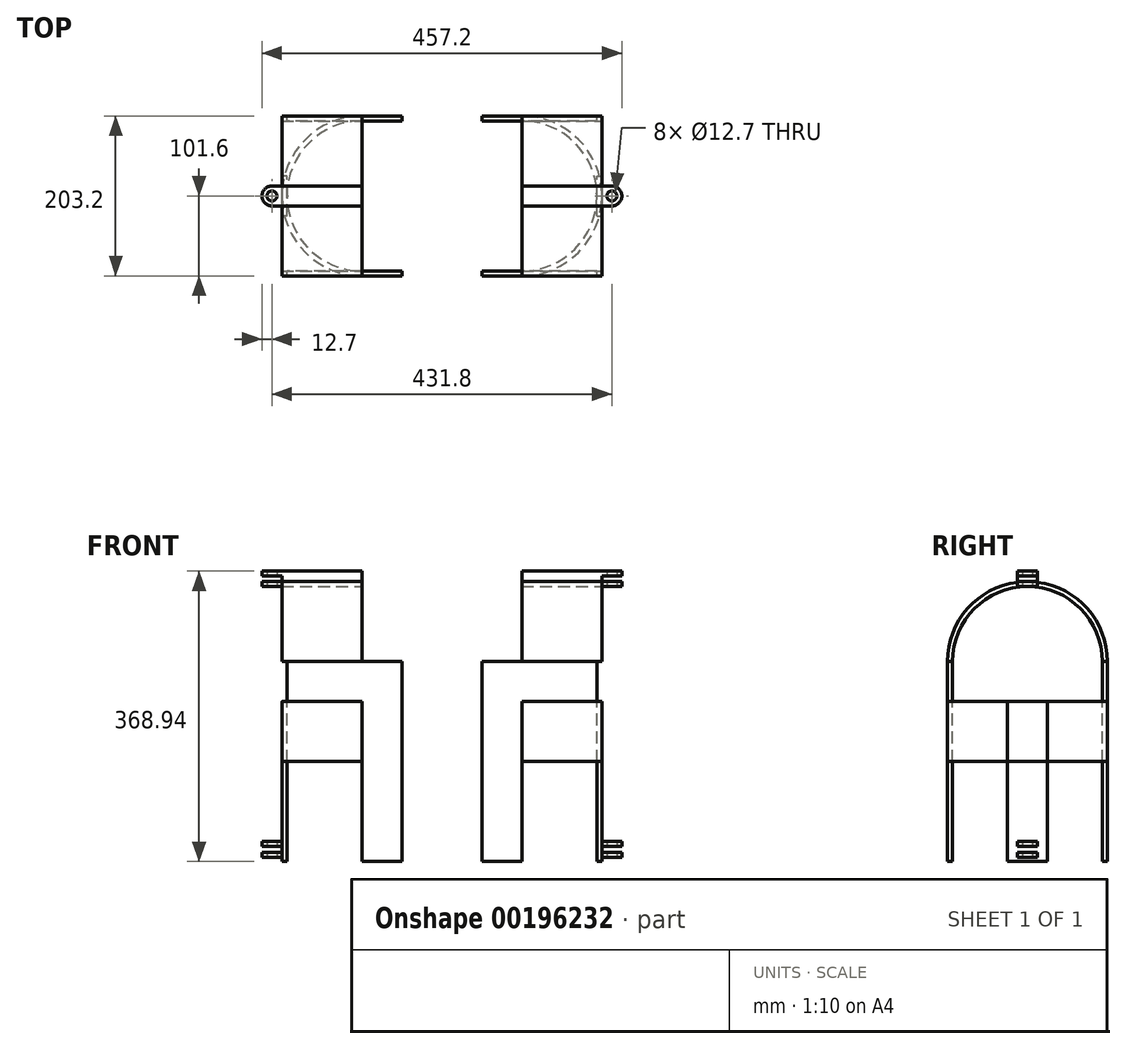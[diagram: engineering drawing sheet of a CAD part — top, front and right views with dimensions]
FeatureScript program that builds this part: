
annotation { "Feature Type Name" : "Feature", "Feature Type Description" : "" }
export const myFeature = defineFeature(function(context is Context, id is Id, definition is map)
    precondition{}
    {
        {
            var Q0;
            Q0=qCreatedBy(makeId("Front.planeOp"),FACE);
            var sketch = newSketch(context, id + "F0", { "sketchPlane" : qUnion([Q0])});
            skLineSegment(sketch, "E0", {"start": v(0, 0) * mm, "end": v(203.2, 0) * mm});
            skLineSegment(sketch, "E1", {"start": v(0, 0) * mm, "end": v(-203.2, 0) * mm});
            skLineSegment(sketch, "E2", {"start": v(0, 0) * mm, "end": v(0, 406.4) * mm});
            skLineSegment(sketch, "E3", {"start": v(0, 406.4) * mm, "end": v(203.2, 406.4) * mm});
            skLineSegment(sketch, "E4", {"start": v(203.2, 406.4) * mm, "end": v(203.2, 0) * mm});
            skLineSegment(sketch, "E5", {"start": v(0, 406.4) * mm, "end": v(-203.2, 406.4) * mm});
            skLineSegment(sketch, "E6", {"start": v(-203.2, 406.4) * mm, "end": v(-203.2, 0) * mm});
            skLineSegment(sketch, "E7", {"start": v(-101.6, 406.4) * mm, "end": v(-101.6, 0) * mm});
            skLineSegment(sketch, "E8", {"start": v(101.6, 0) * mm, "end": v(101.6, 406.4) * mm});
            skLineSegment(sketch, "E9", {"start": v(203.2, 406.4) * mm, "end": v(304.8, 406.4) * mm});
            skLineSegment(sketch, "E10", {"start": v(304.8, 406.4) * mm, "end": v(304.8, 304.8) * mm});
            skLineSegment(sketch, "E11", {"start": v(304.8, 304.8) * mm, "end": v(203.2, 304.8) * mm});
            skLineSegment(sketch, "E12", {"start": v(203.2, 304.8) * mm, "end": v(203.2, 406.4) * mm});
            skLineSegment(sketch, "E13", {"start": v(-203.2, 406.4) * mm, "end": v(-304.8, 406.4) * mm});
            skLineSegment(sketch, "E14", {"start": v(-304.8, 406.4) * mm, "end": v(-304.8, 304.8) * mm});
            skLineSegment(sketch, "E15", {"start": v(-304.8, 304.8) * mm, "end": v(-203.2, 304.8) * mm});
            skLineSegment(sketch, "E16", {"start": v(-203.2, 304.8) * mm, "end": v(-203.2, 406.4) * mm});
            skLineSegment(sketch, "E17", {"start": v(0, 0) * mm, "end": v(0, 50.8) * mm});
            skLineSegment(sketch, "E18", {"start": v(0, 50.8) * mm, "end": v(0, 127) * mm});
            skLineSegment(sketch, "E19", {"start": v(0, 127) * mm, "end": v(0, 177.8) * mm});
            skLineSegment(sketch, "E20", {"start": v(203.2, 304.8) * mm, "end": v(-203.2, 304.8) * mm});
            skLineSegment(sketch, "E21", {"start": v(0, 177.8) * mm, "end": v(0, 254) * mm});
            skLineSegment(sketch, "E22", {"start": v(0, 254) * mm, "end": v(0, 304.8) * mm});
            skLineSegment(sketch, "E23", {"start": v(0, 50.8) * mm, "end": v(-203.2, 50.8) * mm});
            skLineSegment(sketch, "E24", {"start": v(0, 50.8) * mm, "end": v(203.2, 50.8) * mm});
            skLineSegment(sketch, "E25", {"start": v(0, 127) * mm, "end": v(203.2, 127) * mm});
            skLineSegment(sketch, "E26", {"start": v(0, 127) * mm, "end": v(-203.2, 127) * mm});
            skLineSegment(sketch, "E27", {"start": v(0, 177.8) * mm, "end": v(203.2, 177.8) * mm});
            skLineSegment(sketch, "E28", {"start": v(0, 177.8) * mm, "end": v(-203.2, 177.8) * mm});
            skLineSegment(sketch, "E29", {"start": v(0, 254) * mm, "end": v(203.2, 254) * mm});
            skLineSegment(sketch, "E30", {"start": v(0, 254) * mm, "end": v(-203.2, 254) * mm});
            skLineSegment(sketch, "E31", {"start": v(203.2, 0) * mm, "end": v(196.85, 0) * mm});
            skLineSegment(sketch, "E32", {"start": v(196.85, 0) * mm, "end": v(196.85, 304.8) * mm});
            skLineSegment(sketch, "E33", {"start": v(196.85, 304.8) * mm, "end": v(203.2, 304.8) * mm});
            skLineSegment(sketch, "E34", {"start": v(-203.2, 0) * mm, "end": v(-196.85, 0) * mm});
            skLineSegment(sketch, "E35", {"start": v(-196.85, 0) * mm, "end": v(-196.85, 304.8) * mm});
            skLineSegment(sketch, "E36", {"start": v(-196.85, 304.8) * mm, "end": v(-203.2, 304.8) * mm});
            skLineSegment(sketch, "E37", {"start": v(-101.6, 0) * mm, "end": v(-50.8, 0) * mm});
            skLineSegment(sketch, "E38", {"start": v(-50.8, 0) * mm, "end": v(-50.8, 406.4) * mm});
            skLineSegment(sketch, "E39", {"start": v(-50.8, 406.4) * mm, "end": v(-101.6, 406.4) * mm});
            skLineSegment(sketch, "E40", {"start": v(101.6, 406.4) * mm, "end": v(50.8, 406.4) * mm});
            skLineSegment(sketch, "E41", {"start": v(50.8, 406.4) * mm, "end": v(50.8, 0) * mm});
            skLineSegment(sketch, "E42", {"start": v(50.8, 0) * mm, "end": v(101.6, 0) * mm});
            skLineSegment(sketch, "E43", {"start": v(-304.8, 406.4) * mm, "end": v(-304.8, 400.05) * mm});
            skLineSegment(sketch, "E44", {"start": v(-304.8, 400.05) * mm, "end": v(304.8, 400.05) * mm});
            skLineSegment(sketch, "E45", {"start": v(304.8, 400.05) * mm, "end": v(304.8, 406.4) * mm});
            skLineSegment(sketch, "E46.bottom", {"start": v(-304.8, 406.4) * mm, "end": v(-330.2, 406.4) * mm});
            skLineSegment(sketch, "E46.top", {"start": v(-304.8, 400.05) * mm, "end": v(-330.2, 400.05) * mm});
            skLineSegment(sketch, "E46.right", {"start": v(-330.2, 406.4) * mm, "end": v(-330.2, 400.05) * mm});
            skLineSegment(sketch, "E47.bottom", {"start": v(304.8, 406.4) * mm, "end": v(330.2, 406.4) * mm});
            skLineSegment(sketch, "E47.top", {"start": v(304.8, 400.05) * mm, "end": v(330.2, 400.05) * mm});
            skLineSegment(sketch, "E47.left", {"start": v(304.8, 406.4) * mm, "end": v(304.8, 400.05) * mm});
            skLineSegment(sketch, "E47.right", {"start": v(330.2, 406.4) * mm, "end": v(330.2, 400.05) * mm});
            skLineSegment(sketch, "E48", {"start": v(-203.2, 406.4) * mm, "end": v(-203.2, 413.38) * mm});
            skLineSegment(sketch, "E49", {"start": v(-203.2, 413.38) * mm, "end": v(-304.8, 413.38) * mm});
            skLineSegment(sketch, "E50", {"start": v(-304.8, 413.38) * mm, "end": v(-304.8, 406.4) * mm});
            skLineSegment(sketch, "E51.bottom", {"start": v(-203.2, 413.38) * mm, "end": v(-330.2, 413.38) * mm});
            skLineSegment(sketch, "E51.top", {"start": v(-203.2, 419.74) * mm, "end": v(-330.2, 419.74) * mm});
            skLineSegment(sketch, "E51.left", {"start": v(-203.2, 413.38) * mm, "end": v(-203.2, 419.74) * mm});
            skLineSegment(sketch, "E51.right", {"start": v(-330.2, 413.38) * mm, "end": v(-330.2, 419.74) * mm});
            skLineSegment(sketch, "E52", {"start": v(-203.2, 419.74) * mm, "end": v(-101.6, 406.4) * mm});
            skLineSegment(sketch, "E53", {"start": v(203.2, 406.4) * mm, "end": v(203.2, 413.39) * mm});
            skLineSegment(sketch, "E54", {"start": v(203.2, 413.39) * mm, "end": v(304.8, 413.39) * mm});
            skLineSegment(sketch, "E55", {"start": v(304.8, 413.39) * mm, "end": v(304.8, 406.4) * mm});
            skLineSegment(sketch, "E56.bottom", {"start": v(203.2, 413.39) * mm, "end": v(330.2, 413.39) * mm});
            skLineSegment(sketch, "E56.top", {"start": v(203.2, 419.74) * mm, "end": v(330.2, 419.74) * mm});
            skLineSegment(sketch, "E56.left", {"start": v(203.2, 413.39) * mm, "end": v(203.2, 419.74) * mm});
            skLineSegment(sketch, "E56.right", {"start": v(330.2, 413.39) * mm, "end": v(330.2, 419.74) * mm});
            skLineSegment(sketch, "E57", {"start": v(203.2, 419.74) * mm, "end": v(101.6, 406.4) * mm});
            skLineSegment(sketch, "E58", {"start": v(-203.2, 76.2) * mm, "end": v(-203.2, 50.8) * mm});
            skLineSegment(sketch, "E59", {"start": v(-203.2, 50.8) * mm, "end": v(-203.2, 63.5) * mm});
            skLineSegment(sketch, "E60.left", {"start": v(203.2, 50.8) * mm, "end": v(203.2, 76.2) * mm});
            skSolve(sketch);
        }
        {
            var Q0;
            {var subQ0=sQuery(id+"F0.wireOp",EDGE,"E22");Q0=makeQuery(id+"F0.imprint","IMPRINT",FACE,{"disambiguationData":[TD([[makeQuery(id+"F0.imprint","IMPRINT",EDGE,{"derivedFrom":subQ0}),-1.0]])]});}
            var Q1;
            {var subQ0=sQuery(id+"F0.wireOp",EDGE,"E22");Q1=makeQuery(id+"F0.imprint","IMPRINT",FACE,{"disambiguationData":[TD([[makeQuery(id+"F0.imprint","IMPRINT",EDGE,{"derivedFrom":subQ0}),1.0]])]});}
            var Q2;
            {var subQ0=sQuery(id+"F0.wireOp",EDGE,"E20");var subQ1=sQuery(id+"F0.wireOp",EDGE,"E7");var subQ2=makeQuery(id+"F0.imprint","INTERSECT",VERTEX,{"derivedFrom":[subQ1,subQ0]});Q2=makeQuery(id+"F0.imprint","IMPRINT",FACE,{"disambiguationData":[TD([[makeQuery(id+"F0.imprint","IMPRINT",EDGE,{"disambiguationData":[TD([[subQ2,-1.0]])],"derivedFrom":subQ1}),1.0]])]});}
            var Q3;
            {var subQ0=sQuery(id+"F0.wireOp",EDGE,"E30");var subQ1=sQuery(id+"F0.wireOp",EDGE,"E7");var subQ2=makeQuery(id+"F0.imprint","INTERSECT",VERTEX,{"derivedFrom":[subQ1,subQ0]});Q3=makeQuery(id+"F0.imprint","IMPRINT",FACE,{"disambiguationData":[TD([[makeQuery(id+"F0.imprint","IMPRINT",EDGE,{"disambiguationData":[TD([[subQ2,-1.0]])],"derivedFrom":subQ1}),1.0]])]});}
            var Q4;
            {var subQ0=sQuery(id+"F0.wireOp",EDGE,"E29");var subQ1=sQuery(id+"F0.wireOp",EDGE,"E8");var subQ2=makeQuery(id+"F0.imprint","INTERSECT",VERTEX,{"derivedFrom":[subQ1,subQ0]});Q4=makeQuery(id+"F0.imprint","IMPRINT",FACE,{"disambiguationData":[TD([[makeQuery(id+"F0.imprint","IMPRINT",EDGE,{"disambiguationData":[TD([[subQ2,-1.0]])],"derivedFrom":subQ1}),1.0]])]});}
            var Q5;
            {var subQ0=sQuery(id+"F0.wireOp",EDGE,"E27");var subQ1=sQuery(id+"F0.wireOp",EDGE,"E8");var subQ2=makeQuery(id+"F0.imprint","INTERSECT",VERTEX,{"derivedFrom":[subQ1,subQ0]});Q5=makeQuery(id+"F0.imprint","IMPRINT",FACE,{"disambiguationData":[TD([[makeQuery(id+"F0.imprint","IMPRINT",EDGE,{"disambiguationData":[TD([[subQ2,-1.0]])],"derivedFrom":subQ1}),1.0]])]});}
            var Q6;
            {var subQ0=sQuery(id+"F0.wireOp",EDGE,"E25");var subQ1=sQuery(id+"F0.wireOp",EDGE,"E8");var subQ2=makeQuery(id+"F0.imprint","INTERSECT",VERTEX,{"derivedFrom":[subQ1,subQ0]});Q6=makeQuery(id+"F0.imprint","IMPRINT",FACE,{"disambiguationData":[TD([[makeQuery(id+"F0.imprint","IMPRINT",EDGE,{"disambiguationData":[TD([[subQ2,-1.0]])],"derivedFrom":subQ1}),1.0]])]});}
            var Q7;
            {var subQ0=sQuery(id+"F0.wireOp",EDGE,"E19");Q7=makeQuery(id+"F0.imprint","IMPRINT",FACE,{"disambiguationData":[TD([[makeQuery(id+"F0.imprint","IMPRINT",EDGE,{"derivedFrom":subQ0}),-1.0]])]});}
            var Q8;
            {var subQ0=sQuery(id+"F0.wireOp",EDGE,"E19");Q8=makeQuery(id+"F0.imprint","IMPRINT",FACE,{"disambiguationData":[TD([[makeQuery(id+"F0.imprint","IMPRINT",EDGE,{"derivedFrom":subQ0}),1.0]])]});}
            var Q9;
            {var subQ0=sQuery(id+"F0.wireOp",EDGE,"E28");var subQ1=sQuery(id+"F0.wireOp",EDGE,"E7");var subQ2=makeQuery(id+"F0.imprint","INTERSECT",VERTEX,{"derivedFrom":[subQ1,subQ0]});Q9=makeQuery(id+"F0.imprint","IMPRINT",FACE,{"disambiguationData":[TD([[makeQuery(id+"F0.imprint","IMPRINT",EDGE,{"disambiguationData":[TD([[subQ2,-1.0]])],"derivedFrom":subQ1}),1.0]])]});}
            var Q10;
            {var subQ0=sQuery(id+"F0.wireOp",EDGE,"E26");var subQ1=sQuery(id+"F0.wireOp",EDGE,"E7");var subQ2=makeQuery(id+"F0.imprint","INTERSECT",VERTEX,{"derivedFrom":[subQ1,subQ0]});Q10=makeQuery(id+"F0.imprint","IMPRINT",FACE,{"disambiguationData":[TD([[makeQuery(id+"F0.imprint","IMPRINT",EDGE,{"disambiguationData":[TD([[subQ2,-1.0]])],"derivedFrom":subQ1}),1.0]])]});}
            var Q11;
            {var subQ0=sQuery(id+"F0.wireOp",EDGE,"E24");var subQ1=sQuery(id+"F0.wireOp",EDGE,"E8");var subQ2=makeQuery(id+"F0.imprint","INTERSECT",VERTEX,{"derivedFrom":[subQ1,subQ0]});Q11=makeQuery(id+"F0.imprint","IMPRINT",FACE,{"disambiguationData":[TD([[makeQuery(id+"F0.imprint","IMPRINT",EDGE,{"disambiguationData":[TD([[subQ2,-1.0]])],"derivedFrom":subQ1}),1.0]])]});}
            var Q12;
            {var subQ0=sQuery(id+"F0.wireOp",EDGE,"E42");Q12=makeQuery(id+"F0.imprint","IMPRINT",FACE,{"disambiguationData":[TD([[makeQuery(id+"F0.imprint","IMPRINT",EDGE,{"derivedFrom":subQ0}),1.0]])]});}
            var Q13;
            {var subQ0=sQuery(id+"F0.wireOp",EDGE,"E17");Q13=makeQuery(id+"F0.imprint","IMPRINT",FACE,{"disambiguationData":[TD([[makeQuery(id+"F0.imprint","IMPRINT",EDGE,{"derivedFrom":subQ0}),-1.0]])]});}
            var Q14;
            {var subQ0=sQuery(id+"F0.wireOp",EDGE,"E17");Q14=makeQuery(id+"F0.imprint","IMPRINT",FACE,{"disambiguationData":[TD([[makeQuery(id+"F0.imprint","IMPRINT",EDGE,{"derivedFrom":subQ0}),1.0]])]});}
            var Q15;
            {var subQ0=sQuery(id+"F0.wireOp",EDGE,"E37");Q15=makeQuery(id+"F0.imprint","IMPRINT",FACE,{"disambiguationData":[TD([[makeQuery(id+"F0.imprint","IMPRINT",EDGE,{"derivedFrom":subQ0}),1.0]])]});}
            var Q16;
            {var subQ0=sQuery(id+"F0.wireOp",EDGE,"E29");var subQ1=sQuery(id+"F0.wireOp",EDGE,"E8");var subQ2=makeQuery(id+"F0.imprint","INTERSECT",VERTEX,{"derivedFrom":[subQ1,subQ0]});Q16=makeQuery(id+"F0.imprint","IMPRINT",FACE,{"disambiguationData":[TD([[makeQuery(id+"F0.imprint","IMPRINT",EDGE,{"disambiguationData":[TD([[subQ2,-1.0]])],"derivedFrom":subQ1}),-1.0]])]});}
            var Q17;
            {var subQ0=sQuery(id+"F0.wireOp",EDGE,"E20");var subQ1=sQuery(id+"F0.wireOp",EDGE,"E7");var subQ2=makeQuery(id+"F0.imprint","INTERSECT",VERTEX,{"derivedFrom":[subQ1,subQ0]});Q17=makeQuery(id+"F0.imprint","IMPRINT",FACE,{"disambiguationData":[TD([[makeQuery(id+"F0.imprint","IMPRINT",EDGE,{"disambiguationData":[TD([[subQ2,-1.0]])],"derivedFrom":subQ1}),-1.0]])]});}
            extrude(context, id + "F1", {"entities" : qUnion([Q0, Q1, Q2, Q3, Q4, Q5, Q6, Q7, Q8, Q9, Q10, Q11, Q12, Q13, Q14, Q15, Q16, Q17]), "endBound" : BoundingType.SYMMETRIC, "depth" : 6.35 * mm});
        }
        {
            var Q0;
            {var subQ0=sQuery(id+"F0.wireOp",EDGE,"E34");Q0=makeQuery(id+"F0.imprint","IMPRINT",FACE,{"disambiguationData":[TD([[makeQuery(id+"F0.imprint","IMPRINT",EDGE,{"derivedFrom":subQ0}),1.0]])]});}
            var Q1;
            {var subQ0=sQuery(id+"F0.wireOp",EDGE,"E28");var subQ1=sQuery(id+"F0.wireOp",EDGE,"E6");var subQ2=makeQuery(id+"F0.imprint","INTERSECT",VERTEX,{"derivedFrom":[subQ1,subQ0]});Q1=makeQuery(id+"F0.imprint","IMPRINT",FACE,{"disambiguationData":[TD([[makeQuery(id+"F0.imprint","IMPRINT",EDGE,{"disambiguationData":[TD([[subQ2,1.0]])],"derivedFrom":subQ1}),1.0]])]});}
            var Q2;
            Q2=sQuery(id+"F0.wireOp",EDGE,"E7");
            revolve(context, id + "F2", {"entities" : qUnion([Q0, Q1]), "axis" : qUnion([Q2]), "revolveType" : RevolveType.SYMMETRIC, "angle" : 180 * degree});
        }
        {
            var Q0;
            Q0=makeQuery(id+"F1.opExtrude","SWEPT_BODY",BODY,{"disambiguationData":[OSD([sQuery(id+"F0.wireOp",EDGE,"E0"),sQuery(id+"F0.wireOp",EDGE,"E1"),sQuery(id+"F0.wireOp",EDGE,"E7"),sQuery(id+"F0.wireOp",EDGE,"E8"),sQuery(id+"F0.wireOp",EDGE,"E20"),sQuery(id+"F0.wireOp",EDGE,"E23"),sQuery(id+"F0.wireOp",EDGE,"E24"),sQuery(id+"F0.wireOp",EDGE,"E25"),sQuery(id+"F0.wireOp",EDGE,"E26"),sQuery(id+"F0.wireOp",EDGE,"E27"),sQuery(id+"F0.wireOp",EDGE,"E28"),sQuery(id+"F0.wireOp",EDGE,"E29"),sQuery(id+"F0.wireOp",EDGE,"E30"),sQuery(id+"F0.wireOp",EDGE,"E37"),sQuery(id+"F0.wireOp",EDGE,"E38"),sQuery(id+"F0.wireOp",EDGE,"E41"),sQuery(id+"F0.wireOp",EDGE,"E42")])]});
            transform(context, id + "F3", {"entities" : qUnion([Q0]), "transformType" : TransformType.TRANSLATION_3D, "dx" : 0 * mm, "dy" : -98.42 * mm, "dz" : 0 * mm, "makeCopy" : true});
        }
        {
            var Q0;
            Q0=makeQuery(id+"F1.opExtrude","SWEPT_BODY",BODY,{"disambiguationData":[OSD([sQuery(id+"F0.wireOp",EDGE,"E0"),sQuery(id+"F0.wireOp",EDGE,"E1"),sQuery(id+"F0.wireOp",EDGE,"E7"),sQuery(id+"F0.wireOp",EDGE,"E8"),sQuery(id+"F0.wireOp",EDGE,"E20"),sQuery(id+"F0.wireOp",EDGE,"E23"),sQuery(id+"F0.wireOp",EDGE,"E24"),sQuery(id+"F0.wireOp",EDGE,"E25"),sQuery(id+"F0.wireOp",EDGE,"E26"),sQuery(id+"F0.wireOp",EDGE,"E27"),sQuery(id+"F0.wireOp",EDGE,"E28"),sQuery(id+"F0.wireOp",EDGE,"E29"),sQuery(id+"F0.wireOp",EDGE,"E30"),sQuery(id+"F0.wireOp",EDGE,"E37"),sQuery(id+"F0.wireOp",EDGE,"E38"),sQuery(id+"F0.wireOp",EDGE,"E41"),sQuery(id+"F0.wireOp",EDGE,"E42")])]});
            transform(context, id + "F4", {"entities" : qUnion([Q0]), "transformType" : TransformType.TRANSLATION_3D, "dx" : 0 * mm, "dy" : 98.42 * mm, "dz" : 0 * mm, "makeCopy" : false});
        }
        {
            var Q0;
            {var subQ0=sQuery(id+"F0.wireOp",EDGE,"E31");Q0=makeQuery(id+"F0.imprint","IMPRINT",FACE,{"disambiguationData":[TD([[makeQuery(id+"F0.imprint","IMPRINT",EDGE,{"derivedFrom":subQ0}),-1.0]])]});}
            var Q1;
            {var subQ0=sQuery(id+"F0.wireOp",EDGE,"E27");var subQ1=sQuery(id+"F0.wireOp",EDGE,"E4");var subQ2=makeQuery(id+"F0.imprint","INTERSECT",VERTEX,{"derivedFrom":[subQ1,subQ0]});Q1=makeQuery(id+"F0.imprint","IMPRINT",FACE,{"disambiguationData":[TD([[makeQuery(id+"F0.imprint","IMPRINT",EDGE,{"disambiguationData":[TD([[subQ2,1.0]])],"derivedFrom":subQ1}),-1.0]])]});}
            var Q2;
            Q2=sQuery(id+"F0.wireOp",EDGE,"E8");
            revolve(context, id + "F5", {"entities" : qUnion([Q0, Q1]), "axis" : qUnion([Q2]), "revolveType" : RevolveType.SYMMETRIC, "angle" : 180 * degree});
        }
        {
            var Q0;
            {var subQ3=sQuery(id+"F0.wireOp",EDGE,"E7");var subQ5=sQuery(id+"F0.wireOp",EDGE,"E44");var subQ7=makeQuery(id+"F0.imprint","INTERSECT",VERTEX,{"derivedFrom":[subQ3,subQ5]});Q0=makeQuery(id+"F0.imprint","IMPRINT",FACE,{"disambiguationData":[TD([[makeQuery(id+"F0.imprint","IMPRINT",EDGE,{"disambiguationData":[TD([[subQ7,1.0]])],"derivedFrom":subQ5}),1.0]])]});}
            var Q1;
            {var subQ3=sQuery(id+"F0.wireOp",EDGE,"E8");var subQ5=sQuery(id+"F0.wireOp",EDGE,"E44");var subQ6=makeQuery(id+"F0.imprint","INTERSECT",VERTEX,{"derivedFrom":[subQ3,subQ5]});Q1=makeQuery(id+"F0.imprint","IMPRINT",FACE,{"disambiguationData":[TD([[makeQuery(id+"F0.imprint","IMPRINT",EDGE,{"disambiguationData":[TD([[subQ6,-1.0]])],"derivedFrom":subQ5}),1.0]])]});}
            var Q2;
            Q2=sQuery(id+"F0.wireOp",EDGE,"E20");
            revolve(context, id + "F6", {"entities" : qUnion([Q0, Q1]), "axis" : qUnion([Q2]), "revolveType" : RevolveType.SYMMETRIC, "angle" : 180 * degree});
        }
        {
            var Q0;
            Q0=makeQuery(id+"F0.imprint","IMPRINT",FACE,{"disambiguationData":[TD([[makeQuery(id+"F0.imprint","IMPRINT",EDGE,{"derivedFrom":sQuery(id+"F0.wireOp",EDGE,"E47.bottom")}),-1.0]])]});
            var Q1;
            Q1=makeQuery(id+"F0.imprint","IMPRINT",FACE,{"disambiguationData":[TD([[makeQuery(id+"F0.imprint","IMPRINT",EDGE,{"derivedFrom":sQuery(id+"F0.wireOp",EDGE,"E46.bottom")}),1.0]])]});
            var Q2;
            Q2=makeQuery(id+"F0.imprint","IMPRINT",FACE,{"disambiguationData":[TD([[makeQuery(id+"F0.imprint","IMPRINT",EDGE,{"derivedFrom":sQuery(id+"F0.wireOp",EDGE,"E13")}),-1.0]])]});
            var Q3;
            Q3=makeQuery(id+"F0.imprint","IMPRINT",FACE,{"disambiguationData":[TD([[makeQuery(id+"F0.imprint","IMPRINT",EDGE,{"derivedFrom":sQuery(id+"F0.wireOp",EDGE,"E51.top")}),1.0]])]});
            var Q4;
            Q4=makeQuery(id+"F0.imprint","IMPRINT",FACE,{"disambiguationData":[TD([[makeQuery(id+"F0.imprint","IMPRINT",EDGE,{"derivedFrom":sQuery(id+"F0.wireOp",EDGE,"E9")}),1.0]])]});
            var Q5;
            Q5=makeQuery(id+"F0.imprint","IMPRINT",FACE,{"disambiguationData":[TD([[makeQuery(id+"F0.imprint","IMPRINT",EDGE,{"derivedFrom":sQuery(id+"F0.wireOp",EDGE,"E56.top")}),-1.0]])]});
            extrude(context, id + "F7", {"entities" : qUnion([Q0, Q1, Q2, Q3, Q4, Q5]), "endBound" : BoundingType.SYMMETRIC, "depth" : 25.4 * mm});
        }
        {
            var Q0;
            Q0=qCreatedBy(makeId("Top.planeOp"),FACE);
            var sketch = newSketch(context, id + "F8", { "sketchPlane" : qUnion([Q0])});
            skLineSegment(sketch, "E61", {"start": v(0, 0) * mm, "end": v(-304.8, 0) * mm});
            skLineSegment(sketch, "E62", {"start": v(0, 0) * mm, "end": v(304.8, 0) * mm});
            skLineSegment(sketch, "E63", {"start": v(304.8, 0) * mm, "end": v(317.5, 0) * mm});
            skLineSegment(sketch, "E64", {"start": v(-304.8, 0) * mm, "end": v(-317.5, 0) * mm});
            skCircle(sketch, "E65", {"center": v(-317.5, 0) * mm, "radius": 6.35 * mm});
            skCircle(sketch, "E66", {"center": v(-317.5, 0) * mm, "radius": 12.7 * mm});
            skCircle(sketch, "E67", {"center": v(317.5, 0) * mm, "radius": 6.35 * mm});
            skCircle(sketch, "E68", {"center": v(317.5, 0) * mm, "radius": 12.7 * mm});
            skLineSegment(sketch, "E69", {"start": v(304.8, 0) * mm, "end": v(304.8, 12.7) * mm});
            skLineSegment(sketch, "E70.bottom", {"start": v(304.8, 12.7) * mm, "end": v(330.2, 12.7) * mm});
            skLineSegment(sketch, "E70.top", {"start": v(304.8, -12.7) * mm, "end": v(330.2, -12.7) * mm});
            skLineSegment(sketch, "E70.left", {"start": v(304.8, 12.7) * mm, "end": v(304.8, -12.7) * mm});
            skLineSegment(sketch, "E70.right", {"start": v(330.2, 12.7) * mm, "end": v(330.2, -12.7) * mm});
            skLineSegment(sketch, "E71", {"start": v(-304.8, 0) * mm, "end": v(-304.8, 12.7) * mm});
            skLineSegment(sketch, "E72.bottom", {"start": v(-304.8, 12.7) * mm, "end": v(-330.2, 12.7) * mm});
            skLineSegment(sketch, "E72.top", {"start": v(-304.8, -12.7) * mm, "end": v(-330.2, -12.7) * mm});
            skLineSegment(sketch, "E72.left", {"start": v(-304.8, 12.7) * mm, "end": v(-304.8, -12.7) * mm});
            skLineSegment(sketch, "E72.right", {"start": v(-330.2, 12.7) * mm, "end": v(-330.2, -12.7) * mm});
            skSolve(sketch);
        }
        {
            var Q0;
            {var subQ0=sQuery(id+"F8.wireOp",EDGE,"E70.bottom");var subQ1=sQuery(id+"F8.wireOp",EDGE,"E68");var subQ2=makeQuery(id+"F8.imprint","INTERSECT",VERTEX,{"derivedFrom":[subQ1,subQ0]});Q0=makeQuery(id+"F8.imprint","IMPRINT",FACE,{"disambiguationData":[TD([[makeQuery(id+"F8.imprint","IMPRINT",EDGE,{"disambiguationData":[TD([[subQ2,1.0]])],"derivedFrom":subQ1}),-1.0]])]});}
            var Q1;
            {var subQ0=sQuery(id+"F8.wireOp",EDGE,"E70.right");var subQ1=sQuery(id+"F8.wireOp",EDGE,"E68");var subQ2=makeQuery(id+"F8.imprint","INTERSECT",VERTEX,{"derivedFrom":[subQ1,subQ0]});Q1=makeQuery(id+"F8.imprint","IMPRINT",FACE,{"disambiguationData":[TD([[makeQuery(id+"F8.imprint","IMPRINT",EDGE,{"disambiguationData":[TD([[subQ2,1.0]])],"derivedFrom":subQ1}),-1.0]])]});}
            var Q2;
            Q2=makeQuery(id+"F8.imprint","IMPRINT",FACE,{"disambiguationData":[TD([[makeQuery(id+"F8.imprint","IMPRINT",EDGE,{"derivedFrom":sQuery(id+"F8.wireOp",EDGE,"E67")}),1.0]])]});
            var Q3;
            {var subQ0=sQuery(id+"F8.wireOp",EDGE,"E72.bottom");var subQ1=sQuery(id+"F8.wireOp",EDGE,"E66");var subQ2=makeQuery(id+"F8.imprint","INTERSECT",VERTEX,{"derivedFrom":[subQ1,subQ0]});Q3=makeQuery(id+"F8.imprint","IMPRINT",FACE,{"disambiguationData":[TD([[makeQuery(id+"F8.imprint","IMPRINT",EDGE,{"disambiguationData":[TD([[subQ2,-1.0]])],"derivedFrom":subQ1}),-1.0]])]});}
            var Q4;
            Q4=makeQuery(id+"F8.imprint","IMPRINT",FACE,{"disambiguationData":[TD([[makeQuery(id+"F8.imprint","IMPRINT",EDGE,{"derivedFrom":sQuery(id+"F8.wireOp",EDGE,"E65")}),1.0]])]});
            var Q5;
            {var subQ0=sQuery(id+"F8.wireOp",EDGE,"E72.right");var subQ1=sQuery(id+"F8.wireOp",EDGE,"E66");var subQ2=makeQuery(id+"F8.imprint","INTERSECT",VERTEX,{"derivedFrom":[subQ1,subQ0]});Q5=makeQuery(id+"F8.imprint","IMPRINT",FACE,{"disambiguationData":[TD([[makeQuery(id+"F8.imprint","IMPRINT",EDGE,{"disambiguationData":[TD([[subQ2,-1.0]])],"derivedFrom":subQ1}),-1.0]])]});}
            extrude(context, id + "F9", {"entities" : qUnion([Q0, Q1, Q2, Q3, Q4, Q5]), "depth" : 508 * mm});
        }
        {
            var Q0;
            Q0=makeQuery(id+"F9.opExtrude","SWEPT_BODY",BODY,{"disambiguationData":[OSD([sQuery(id+"F8.wireOp",EDGE,"E65")])]});
            var Q1;
            Q1=makeQuery(id+"F9.opExtrude","SWEPT_BODY",BODY,{"disambiguationData":[OSD([sQuery(id+"F8.wireOp",EDGE,"E66"),sQuery(id+"F8.wireOp",EDGE,"E72.top"),sQuery(id+"F8.wireOp",EDGE,"E72.right")])]});
            var Q2;
            Q2=makeQuery(id+"F9.opExtrude","SWEPT_BODY",BODY,{"disambiguationData":[OSD([sQuery(id+"F8.wireOp",EDGE,"E68"),sQuery(id+"F8.wireOp",EDGE,"E70.top"),sQuery(id+"F8.wireOp",EDGE,"E70.right")])]});
            var Q3;
            Q3=makeQuery(id+"F9.opExtrude","SWEPT_BODY",BODY,{"disambiguationData":[OSD([sQuery(id+"F8.wireOp",EDGE,"E68"),sQuery(id+"F8.wireOp",EDGE,"E70.bottom"),sQuery(id+"F8.wireOp",EDGE,"E70.right")])]});
            var Q4;
            Q4=makeQuery(id+"F9.opExtrude","SWEPT_BODY",BODY,{"disambiguationData":[OSD([sQuery(id+"F8.wireOp",EDGE,"E67")])]});
            var Q5;
            Q5=makeQuery(id+"F9.opExtrude","SWEPT_BODY",BODY,{"disambiguationData":[OSD([sQuery(id+"F8.wireOp",EDGE,"E66"),sQuery(id+"F8.wireOp",EDGE,"E72.bottom"),sQuery(id+"F8.wireOp",EDGE,"E72.right")])]});
            var Q6;
            Q6=makeQuery(id+"F7.opExtrude","SWEPT_BODY",BODY,{"disambiguationData":[OSD([sQuery(id+"F0.wireOp",EDGE,"E13"),sQuery(id+"F0.wireOp",EDGE,"E48"),sQuery(id+"F0.wireOp",EDGE,"E50"),sQuery(id+"F0.wireOp",EDGE,"E51.bottom"),sQuery(id+"F0.wireOp",EDGE,"E51.top"),sQuery(id+"F0.wireOp",EDGE,"E51.left"),sQuery(id+"F0.wireOp",EDGE,"E51.right")])]});
            var Q7;
            Q7=makeQuery(id+"F7.opExtrude","SWEPT_BODY",BODY,{"disambiguationData":[OSD([sQuery(id+"F0.wireOp",EDGE,"E46.bottom"),sQuery(id+"F0.wireOp",EDGE,"E46.top"),sQuery(id+"F0.wireOp",EDGE,"E43"),sQuery(id+"F0.wireOp",EDGE,"E46.right")])]});
            var Q8;
            Q8=makeQuery(id+"F7.opExtrude","SWEPT_BODY",BODY,{"disambiguationData":[OSD([sQuery(id+"F0.wireOp",EDGE,"E9"),sQuery(id+"F0.wireOp",EDGE,"E53"),sQuery(id+"F0.wireOp",EDGE,"E55"),sQuery(id+"F0.wireOp",EDGE,"E56.bottom"),sQuery(id+"F0.wireOp",EDGE,"E56.top"),sQuery(id+"F0.wireOp",EDGE,"E56.left"),sQuery(id+"F0.wireOp",EDGE,"E56.right")])]});
            var Q9;
            Q9=makeQuery(id+"F7.opExtrude","SWEPT_BODY",BODY,{"disambiguationData":[OSD([sQuery(id+"F0.wireOp",EDGE,"E47.bottom"),sQuery(id+"F0.wireOp",EDGE,"E47.top"),sQuery(id+"F0.wireOp",EDGE,"E47.left"),sQuery(id+"F0.wireOp",EDGE,"E47.right")])]});
            booleanBodies(context, id + "F10", {"operationType" : BooleanOperationType.SUBTRACTION, "tools" : qUnion([Q0, Q1, Q2, Q3, Q4, Q5]), "targets" : qUnion([Q6, Q7, Q8, Q9])});
        }
        {
            var Q0;
            Q0=makeQuery(id+"F7.opExtrude","SWEPT_BODY",BODY,{"disambiguationData":[OSD([sQuery(id+"F0.wireOp",EDGE,"E13"),sQuery(id+"F0.wireOp",EDGE,"E48"),sQuery(id+"F0.wireOp",EDGE,"E50"),sQuery(id+"F0.wireOp",EDGE,"E51.bottom"),sQuery(id+"F0.wireOp",EDGE,"E51.top"),sQuery(id+"F0.wireOp",EDGE,"E51.left"),sQuery(id+"F0.wireOp",EDGE,"E51.right")])]});
            var Q1;
            Q1=makeQuery(id+"F7.opExtrude","SWEPT_BODY",BODY,{"disambiguationData":[OSD([sQuery(id+"F0.wireOp",EDGE,"E46.bottom"),sQuery(id+"F0.wireOp",EDGE,"E46.top"),sQuery(id+"F0.wireOp",EDGE,"E43"),sQuery(id+"F0.wireOp",EDGE,"E46.right")])]});
            transform(context, id + "F11", {"entities" : qUnion([Q0, Q1]), "transformType" : TransformType.TRANSLATION_3D, "dx" : 101.6 * mm, "dy" : 0 * mm, "dz" : 0 * mm, "makeCopy" : false});
        }
        {
            var Q0;
            Q0=makeQuery(id+"F7.opExtrude","SWEPT_BODY",BODY,{"disambiguationData":[OSD([sQuery(id+"F0.wireOp",EDGE,"E9"),sQuery(id+"F0.wireOp",EDGE,"E53"),sQuery(id+"F0.wireOp",EDGE,"E55"),sQuery(id+"F0.wireOp",EDGE,"E56.bottom"),sQuery(id+"F0.wireOp",EDGE,"E56.top"),sQuery(id+"F0.wireOp",EDGE,"E56.left"),sQuery(id+"F0.wireOp",EDGE,"E56.right")])]});
            var Q1;
            Q1=makeQuery(id+"F7.opExtrude","SWEPT_BODY",BODY,{"disambiguationData":[OSD([sQuery(id+"F0.wireOp",EDGE,"E47.bottom"),sQuery(id+"F0.wireOp",EDGE,"E47.top"),sQuery(id+"F0.wireOp",EDGE,"E47.left"),sQuery(id+"F0.wireOp",EDGE,"E47.right")])]});
            transform(context, id + "F12", {"entities" : qUnion([Q0, Q1]), "transformType" : TransformType.TRANSLATION_3D, "dx" : -101.6 * mm, "dy" : 0 * mm, "dz" : 0 * mm, "makeCopy" : false});
        }
        {
            var Q0;
            {var subQ0=sQuery(id+"F0.wireOp",EDGE,"E34");Q0=makeQuery(id+"F0.imprint","IMPRINT",FACE,{"disambiguationData":[TD([[makeQuery(id+"F0.imprint","IMPRINT",EDGE,{"derivedFrom":subQ0}),1.0]])]});}
            var Q1;
            {var subQ0=sQuery(id+"F0.wireOp",EDGE,"E23");var subQ1=sQuery(id+"F0.wireOp",EDGE,"E6");var subQ2=makeQuery(id+"F0.imprint","INTERSECT",VERTEX,{"derivedFrom":[subQ1,subQ0]});Q1=makeQuery(id+"F0.imprint","IMPRINT",FACE,{"disambiguationData":[TD([[makeQuery(id+"F0.imprint","IMPRINT",EDGE,{"disambiguationData":[TD([[subQ2,1.0]])],"derivedFrom":subQ1}),1.0]])]});}
            var Q2;
            {var subQ0=sQuery(id+"F0.wireOp",EDGE,"E26");var subQ1=sQuery(id+"F0.wireOp",EDGE,"E6");var subQ2=makeQuery(id+"F0.imprint","INTERSECT",VERTEX,{"derivedFrom":[subQ1,subQ0]});Q2=makeQuery(id+"F0.imprint","IMPRINT",FACE,{"disambiguationData":[TD([[makeQuery(id+"F0.imprint","IMPRINT",EDGE,{"disambiguationData":[TD([[subQ2,1.0]])],"derivedFrom":subQ1}),1.0]])]});}
            var Q3;
            {var subQ0=sQuery(id+"F0.wireOp",EDGE,"E28");var subQ1=sQuery(id+"F0.wireOp",EDGE,"E6");var subQ2=makeQuery(id+"F0.imprint","INTERSECT",VERTEX,{"derivedFrom":[subQ1,subQ0]});Q3=makeQuery(id+"F0.imprint","IMPRINT",FACE,{"disambiguationData":[TD([[makeQuery(id+"F0.imprint","IMPRINT",EDGE,{"disambiguationData":[TD([[subQ2,1.0]])],"derivedFrom":subQ1}),1.0]])]});}
            var Q4;
            {var subQ0=sQuery(id+"F0.wireOp",EDGE,"E31");Q4=makeQuery(id+"F0.imprint","IMPRINT",FACE,{"disambiguationData":[TD([[makeQuery(id+"F0.imprint","IMPRINT",EDGE,{"derivedFrom":subQ0}),-1.0]])]});}
            var Q5;
            {var subQ0=sQuery(id+"F0.wireOp",EDGE,"E24");var subQ1=sQuery(id+"F0.wireOp",EDGE,"E4");var subQ2=makeQuery(id+"F0.imprint","INTERSECT",VERTEX,{"derivedFrom":[subQ1,subQ0]});Q5=makeQuery(id+"F0.imprint","IMPRINT",FACE,{"disambiguationData":[TD([[makeQuery(id+"F0.imprint","IMPRINT",EDGE,{"disambiguationData":[TD([[subQ2,1.0]])],"derivedFrom":subQ1}),-1.0]])]});}
            var Q6;
            {var subQ0=sQuery(id+"F0.wireOp",EDGE,"E25");var subQ1=sQuery(id+"F0.wireOp",EDGE,"E4");var subQ2=makeQuery(id+"F0.imprint","INTERSECT",VERTEX,{"derivedFrom":[subQ1,subQ0]});Q6=makeQuery(id+"F0.imprint","IMPRINT",FACE,{"disambiguationData":[TD([[makeQuery(id+"F0.imprint","IMPRINT",EDGE,{"disambiguationData":[TD([[subQ2,1.0]])],"derivedFrom":subQ1}),-1.0]])]});}
            var Q7;
            {var subQ0=sQuery(id+"F0.wireOp",EDGE,"E27");var subQ1=sQuery(id+"F0.wireOp",EDGE,"E4");var subQ2=makeQuery(id+"F0.imprint","INTERSECT",VERTEX,{"derivedFrom":[subQ1,subQ0]});Q7=makeQuery(id+"F0.imprint","IMPRINT",FACE,{"disambiguationData":[TD([[makeQuery(id+"F0.imprint","IMPRINT",EDGE,{"disambiguationData":[TD([[subQ2,1.0]])],"derivedFrom":subQ1}),-1.0]])]});}
            var Q8;
            {var subQ8=sQuery(id+"F0.wireOp",EDGE,"E58");Q8=makeQuery(id+"F0.imprint","IMPRINT",FACE,{"disambiguationData":[TD([[makeQuery(id+"F0.imprint","IMPRINT",EDGE,{"derivedFrom":subQ8}),1.0]])]});}
            var Q9;
            {var subQ3=sQuery(id+"F0.wireOp",EDGE,"E25");var subQ6=sQuery(id+"F0.wireOp",EDGE,"E4");var subQ9=makeQuery(id+"F0.imprint","INTERSECT",VERTEX,{"derivedFrom":[subQ6,subQ3]});Q9=makeQuery(id+"F0.imprint","IMPRINT",FACE,{"disambiguationData":[TD([[makeQuery(id+"F0.imprint","IMPRINT",EDGE,{"disambiguationData":[TD([[subQ9,1.0]])],"derivedFrom":subQ3}),-1.0]])]});}
            extrude(context, id + "F13", {"entities" : qUnion([Q0, Q1, Q2, Q3, Q4, Q5, Q6, Q7, Q8, Q9]), "endBound" : BoundingType.SYMMETRIC, "depth" : 50.8 * mm});
        }
        {
            var Q0;
            Q0=makeQuery(id+"F7.opExtrude","SWEPT_BODY",BODY,{"disambiguationData":[OSD([sQuery(id+"F0.wireOp",EDGE,"E47.bottom"),sQuery(id+"F0.wireOp",EDGE,"E47.top"),sQuery(id+"F0.wireOp",EDGE,"E47.left"),sQuery(id+"F0.wireOp",EDGE,"E47.right")])]});
            var Q1;
            Q1=makeQuery(id+"F7.opExtrude","SWEPT_BODY",BODY,{"disambiguationData":[OSD([sQuery(id+"F0.wireOp",EDGE,"E46.bottom"),sQuery(id+"F0.wireOp",EDGE,"E46.top"),sQuery(id+"F0.wireOp",EDGE,"E43"),sQuery(id+"F0.wireOp",EDGE,"E46.right")])]});
            transform(context, id + "F14", {"entities" : qUnion([Q0, Q1]), "transformType" : TransformType.TRANSLATION_3D, "dx" : 0 * mm, "dy" : 0 * mm, "dz" : -330.2 * mm, "makeCopy" : true});
        }
        {
            var Q0;
            Q0=makeQuery(id+"F14.opPattern","COPY",BODY,{"derivedFrom":makeQuery(id+"F7.opExtrude","SWEPT_BODY",BODY,{"disambiguationData":[OSD([sQuery(id+"F0.wireOp",EDGE,"E47.bottom"),sQuery(id+"F0.wireOp",EDGE,"E47.top"),sQuery(id+"F0.wireOp",EDGE,"E47.left"),sQuery(id+"F0.wireOp",EDGE,"E47.right")])]}),"instanceName":"1"});
            var Q1;
            Q1=makeQuery(id+"F14.opPattern","COPY",BODY,{"derivedFrom":makeQuery(id+"F7.opExtrude","SWEPT_BODY",BODY,{"disambiguationData":[OSD([sQuery(id+"F0.wireOp",EDGE,"E46.bottom"),sQuery(id+"F0.wireOp",EDGE,"E46.top"),sQuery(id+"F0.wireOp",EDGE,"E43"),sQuery(id+"F0.wireOp",EDGE,"E46.right")])]}),"instanceName":"1"});
            transform(context, id + "F15", {"entities" : qUnion([Q0, Q1]), "transformType" : TransformType.TRANSLATION_3D, "dx" : 0 * mm, "dy" : 0 * mm, "dz" : -13.97 * mm, "makeCopy" : true});
        }
    });
